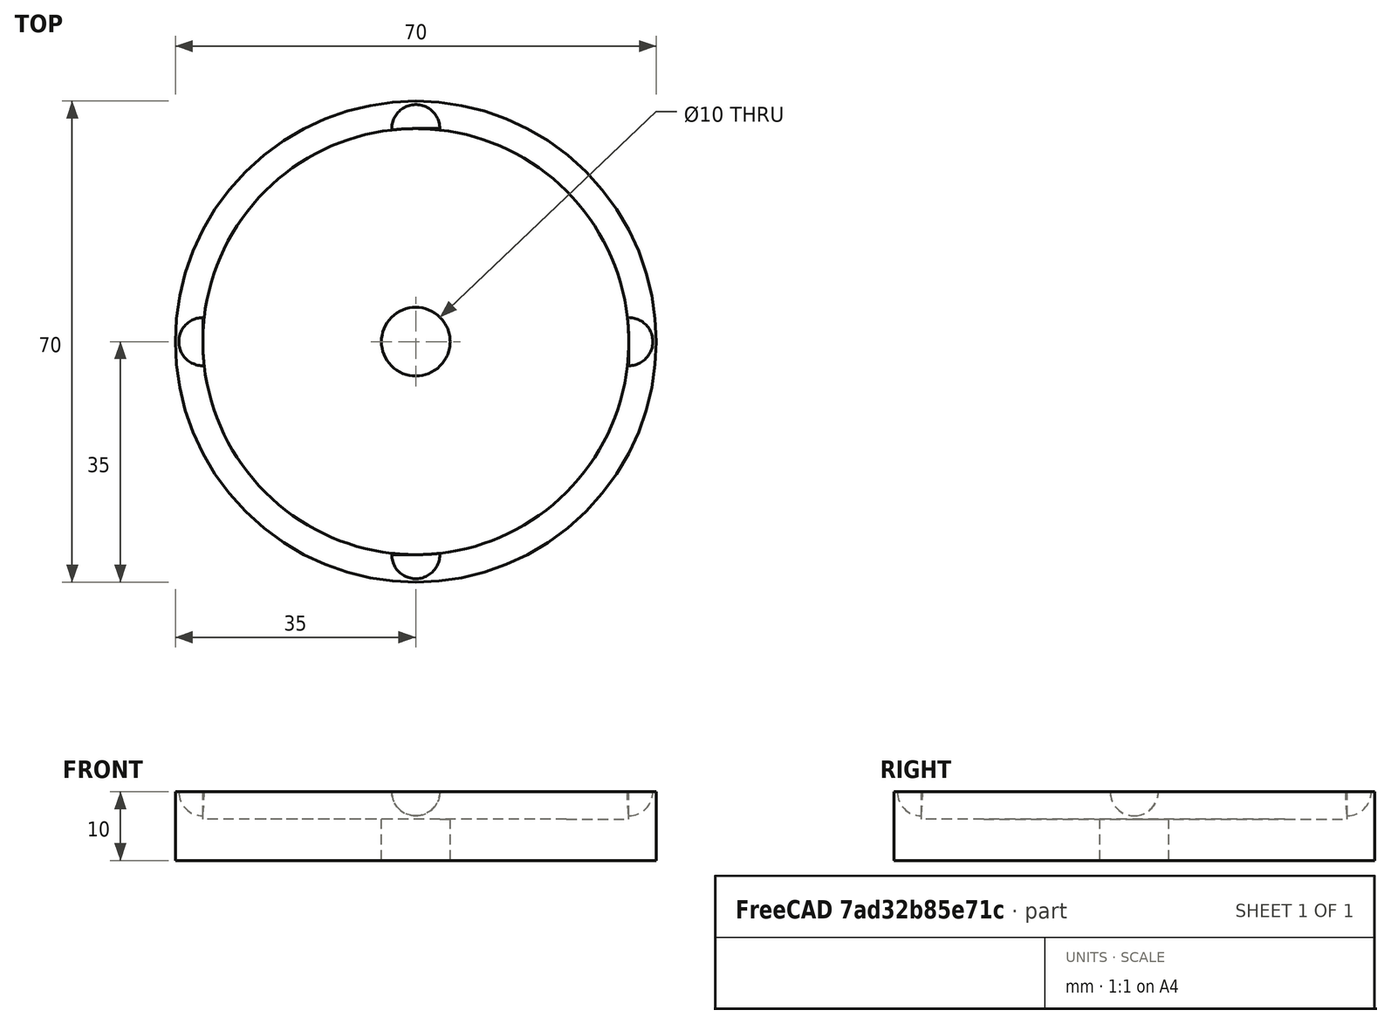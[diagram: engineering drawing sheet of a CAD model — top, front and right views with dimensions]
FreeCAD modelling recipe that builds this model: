
FCSTD DOCUMENT  (FreeCAD 0.19R24291 (Git))
Label: cenicero
License: All rights reserved
LicenseURL: http://en.wikipedia.org/wiki/All_rights_reserved
objects: Part::Cylinder×9, Part::Cut×9, Part::MultiFuse×7, Part::FeaturePython×4, Part::Sphere×4, Part::Box×4, Part::MultiCommon×4
note: 41 computed .brp shape members not serialized (recipe doc carries the construction recipe); baked Part::Feature solids carry a one-line shape summary decoded from their .brp

FEATURE [Part::FeaturePython] Tube  # WARN: FeaturePython — macro-defined, semantics opaque (R4)
  AttacherType = Attacher::AttachEngine3D
  Height = 10
  InnerRadius = 31
  OuterRadius = 35
FEATURE [Part::Cylinder] Cylinder  label="Cilindro"
  Angle = 360
  AttacherType = Attacher::AttachEngine3D
  Height = 6
  Radius = 31
FEATURE [Part::Cylinder] Cylinder001  label="Cilindro001"
  Angle = 360
  AttacherType = Attacher::AttachEngine3D
  Height = 10
  Radius = 4
FEATURE [Part::Cut] Cut
  Base = -> Cylinder
  Tool = -> Cylinder001
FEATURE [Part::Sphere] Sphere  label="Esfera"
  Angle1 = -90
  Angle2 = 90
  Angle3 = 360
  AttacherType = Attacher::AttachEngine3D
  Placement = pos=(0,31,10) rot=(0,0,1;0rad)
  Radius = 3.5
FEATURE [Part::Cut] Cut001
  Base = -> Tube
  Tool = -> Sphere
FEATURE [Part::Box] Box  label="Cubo"
  AttacherType = Attacher::AttachEngine3D
  Height = 10
  Length = 100
  Placement = pos=(0,0,0) rot=(0,0,1;0.785398rad)
  Width = 100
FEATURE [Part::MultiFuse] Fusion
  Shapes = -> [Cut,Cut001]
FEATURE [Part::MultiCommon] Common
  Shapes = -> [Fusion,Box]
FEATURE [Part::FeaturePython] Tube001  # WARN: FeaturePython — macro-defined, semantics opaque (R4)
  AttacherType = Attacher::AttachEngine3D
  Height = 10
  InnerRadius = 31
  OuterRadius = 35
FEATURE [Part::Cylinder] Cylinder002  label="Cilindro002"
  Angle = 360
  AttacherType = Attacher::AttachEngine3D
  Height = 10
  Radius = 4
FEATURE [Part::Box] Box001  label="Cubo001"
  AttacherType = Attacher::AttachEngine3D
  Height = 10
  Length = 100
  Placement = pos=(0,0,0) rot=(0,0,1;0.785398rad)
  Width = 100
FEATURE [Part::Cylinder] Cylinder003  label="Cilindro003"
  Angle = 360
  AttacherType = Attacher::AttachEngine3D
  Height = 6
  Radius = 31
FEATURE [Part::Cut] Cut002
  Base = -> Cylinder003
  Tool = -> Cylinder002
FEATURE [Part::Sphere] Sphere001  label="Esfera001"
  Angle1 = -90
  Angle2 = 90
  Angle3 = 360
  AttacherType = Attacher::AttachEngine3D
  Placement = pos=(0,31,10) rot=(0,0,1;0rad)
  Radius = 3.5
FEATURE [Part::Cut] Cut003
  Base = -> Tube001
  Tool = -> Sphere001
FEATURE [Part::MultiFuse] Fusion001
  Shapes = -> [Cut002,Cut003]
FEATURE [Part::MultiCommon] Common001
  Placement = pos=(0,0,0) rot=(0,0,1;1.5708rad)
  Shapes = -> [Fusion001,Box001]
FEATURE [Part::MultiFuse] Fusion002
  Placement = pos=(0,0,0) rot=(0,0,1;3.14159rad)
  Shapes = -> [Common,Common001]
FEATURE [Part::Sphere] Sphere002  label="Esfera002"
  Angle1 = -90
  Angle2 = 90
  Angle3 = 360
  AttacherType = Attacher::AttachEngine3D
  Placement = pos=(0,31,10) rot=(0,0,1;0rad)
  Radius = 3.5
FEATURE [Part::FeaturePython] Tube002  # WARN: FeaturePython — macro-defined, semantics opaque (R4)
  AttacherType = Attacher::AttachEngine3D
  Height = 10
  InnerRadius = 31
  OuterRadius = 35
FEATURE [Part::Cut] Cut007
  Base = -> Tube002
  Tool = -> Sphere002
FEATURE [Part::FeaturePython] Tube003  # WARN: FeaturePython — macro-defined, semantics opaque (R4)
  AttacherType = Attacher::AttachEngine3D
  Height = 10
  InnerRadius = 31
  OuterRadius = 35
FEATURE [Part::Cylinder] Cylinder004  label="Cilindro004"
  Angle = 360
  AttacherType = Attacher::AttachEngine3D
  Height = 10
  Radius = 4
FEATURE [Part::Cylinder] Cylinder005  label="Cilindro005"
  Angle = 360
  AttacherType = Attacher::AttachEngine3D
  Height = 10
  Radius = 4
FEATURE [Part::Box] Box002  label="Cubo002"
  AttacherType = Attacher::AttachEngine3D
  Height = 10
  Length = 100
  Placement = pos=(0,0,0) rot=(0,0,1;0.785398rad)
  Width = 100
FEATURE [Part::Cylinder] Cylinder006  label="Cilindro006"
  Angle = 360
  AttacherType = Attacher::AttachEngine3D
  Height = 6
  Radius = 31
FEATURE [Part::Cut] Cut006
  Base = -> Cylinder006
  Tool = -> Cylinder005
FEATURE [Part::MultiFuse] Fusion004
  Shapes = -> [Cut006,Cut007]
FEATURE [Part::MultiCommon] Common002
  Placement = pos=(0,0,0) rot=(0,0,1;1.5708rad)
  Shapes = -> [Fusion004,Box002]
FEATURE [Part::Box] Box003  label="Cubo003"
  AttacherType = Attacher::AttachEngine3D
  Height = 10
  Length = 100
  Placement = pos=(0,0,0) rot=(0,0,1;0.785398rad)
  Width = 100
FEATURE [Part::Cylinder] Cylinder007  label="Cilindro007"
  Angle = 360
  AttacherType = Attacher::AttachEngine3D
  Height = 6
  Radius = 31
FEATURE [Part::Cut] Cut004
  Base = -> Cylinder007
  Tool = -> Cylinder004
FEATURE [Part::Sphere] Sphere003  label="Esfera003"
  Angle1 = -90
  Angle2 = 90
  Angle3 = 360
  AttacherType = Attacher::AttachEngine3D
  Placement = pos=(0,31,10) rot=(0,0,1;0rad)
  Radius = 3.5
FEATURE [Part::Cut] Cut005
  Base = -> Tube003
  Tool = -> Sphere003
FEATURE [Part::MultiFuse] Fusion005
  Shapes = -> [Cut004,Cut005]
FEATURE [Part::MultiCommon] Common003
  Shapes = -> [Fusion005,Box003]
FEATURE [Part::MultiFuse] Fusion003
  Shapes = -> [Common003,Common002]
FEATURE [Part::MultiFuse] Fusion006
  Shapes = -> [Fusion003,Fusion002]
FEATURE [Part::Cylinder] Cylinder008  label="Cilindro008"
  Angle = 360
  AttacherType = Attacher::AttachEngine3D
  Height = 10
  Radius = 5
FEATURE [Part::Cut] Cut008
  Base = -> Fusion006
  Tool = -> Cylinder008
